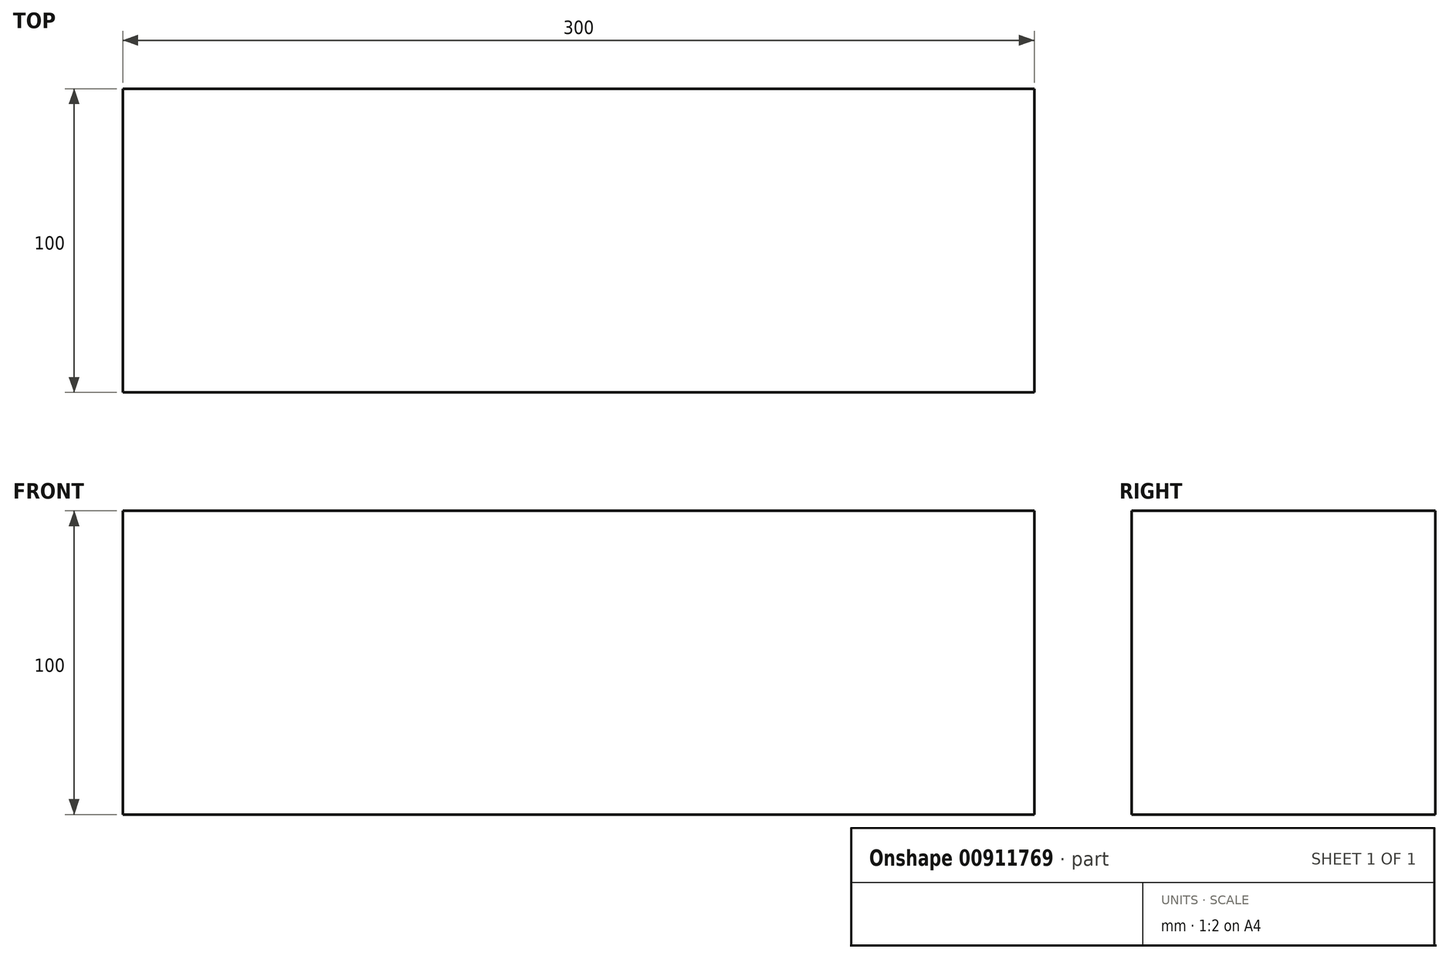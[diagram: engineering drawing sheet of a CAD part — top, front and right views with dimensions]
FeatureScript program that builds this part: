
annotation { "Feature Type Name" : "Feature", "Feature Type Description" : "" }
export const myFeature = defineFeature(function(context is Context, id is Id, definition is map)
    precondition{}
    {
        {
            var Q0;
            Q0=qCreatedBy(makeId("Front.planeOp"),FACE);
            var sketch = newSketch(context, id + "F0", { "sketchPlane" : qUnion([Q0])});
            skLineSegment(sketch, "E0.bottom", {"start": v(-150, 50) * mm, "end": v(150, 50) * mm});
            skLineSegment(sketch, "E0.top", {"start": v(-150, -50) * mm, "end": v(150, -50) * mm});
            skLineSegment(sketch, "E0.left", {"start": v(-150, 50) * mm, "end": v(-150, -50) * mm});
            skLineSegment(sketch, "E0.right", {"start": v(150, 50) * mm, "end": v(150, -50) * mm});
            skPoint(sketch, "E0.middle", {"position": v(0, 0) * mm});
            skSolve(sketch);
        }
        {
            var Q0;
            Q0=makeQuery(id+"F0.imprint","IMPRINT",FACE,{"disambiguationData":[TD([[makeQuery(id+"F0.imprint","IMPRINT",EDGE,{"derivedFrom":sQuery(id+"F0.wireOp",EDGE,"E0.bottom")}),-1.0]])]});
            extrude(context, id + "F1", {"entities" : qUnion([Q0]), "depth" : 100 * mm, "offsetDistance" : 25 * mm});
        }
    });
